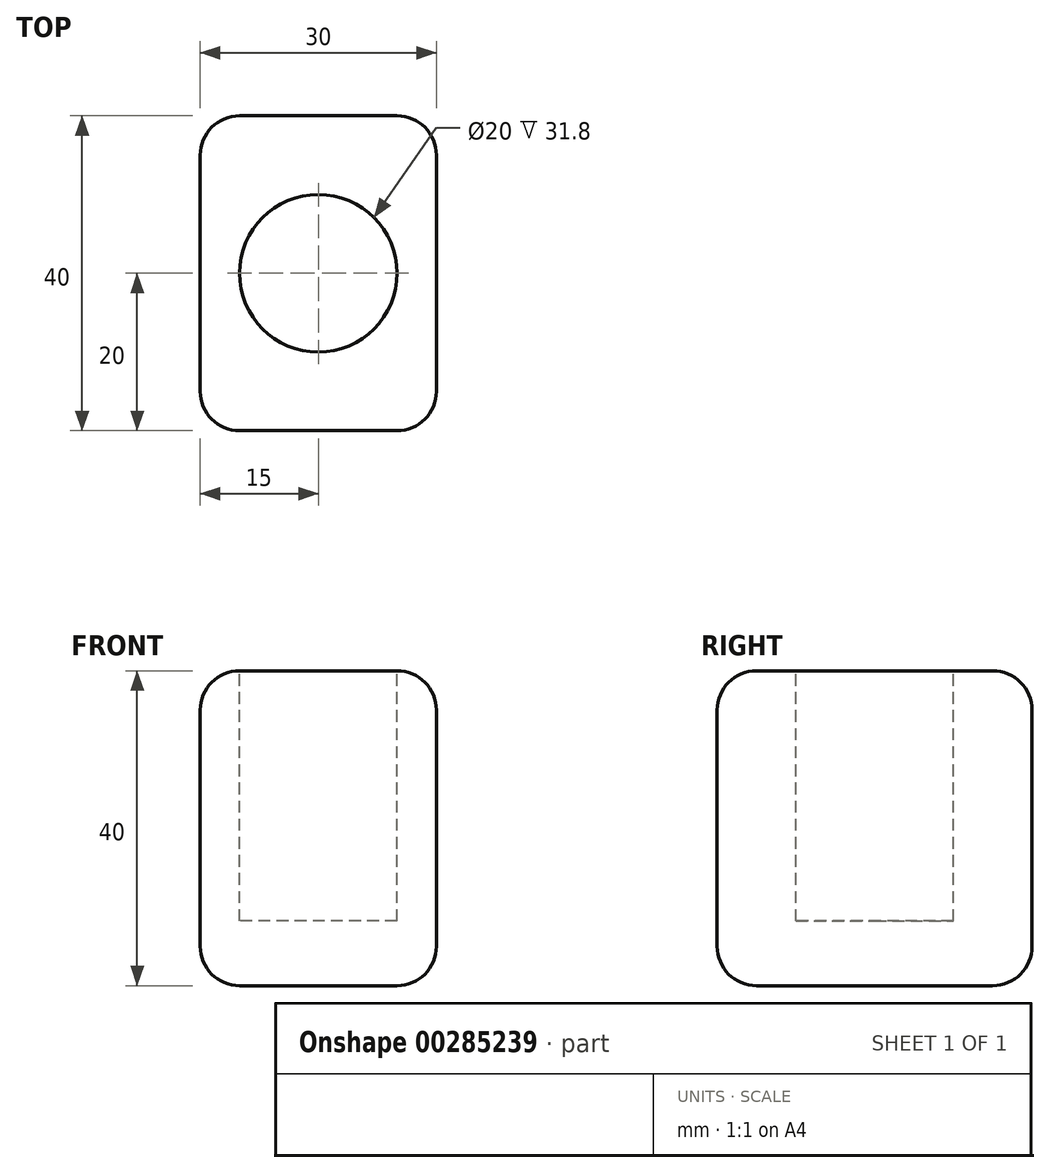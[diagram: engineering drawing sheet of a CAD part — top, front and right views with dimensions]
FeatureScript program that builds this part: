
annotation { "Feature Type Name" : "Feature", "Feature Type Description" : "" }
export const myFeature = defineFeature(function(context is Context, id is Id, definition is map)
    precondition{}
    {
        {
            var Q0;
            Q0=qCreatedBy(makeId("Top.planeOp"),FACE);
            var sketch = newSketch(context, id + "F0", { "sketchPlane" : qUnion([Q0])});
            skLineSegment(sketch, "E0.bottom", {"start": v(0, 0) * mm, "end": v(30, 0) * mm});
            skLineSegment(sketch, "E0.top", {"start": v(0, 40) * mm, "end": v(30, 40) * mm});
            skLineSegment(sketch, "E0.left", {"start": v(0, 0) * mm, "end": v(0, 40) * mm});
            skLineSegment(sketch, "E0.right", {"start": v(30, 0) * mm, "end": v(30, 40) * mm});
            skSolve(sketch);
        }
        {
            var Q0;
            Q0 = qSketchRegion(id + "F0", true);
            extrude(context, id + "F1", {"entities" : qUnion([Q0]), "depth" : 40 * mm});
        }
        {
            var Q0;
            Q0=makeQuery(id+"F1.opExtrude","CAP_FACE",FACE,{"disambiguationData":[OSD([sQuery(id+"F0.wireOp",EDGE,"E0.bottom"),sQuery(id+"F0.wireOp",EDGE,"E0.top"),sQuery(id+"F0.wireOp",EDGE,"E0.left"),sQuery(id+"F0.wireOp",EDGE,"E0.right")])],"isStart":false});
            var sketch = newSketch(context, id + "F2", { "sketchPlane" : qUnion([Q0])});
            skCircle(sketch, "E1", {"center": v(15, 20) * mm, "radius": 10 * mm});
            skPoint(sketch, "E1.centerSnap0", {"position": v(30, 20) * mm});
            skPoint(sketch, "E1.centerSnap1", {"position": v(15, 40) * mm});
            skSolve(sketch);
        }
        {
            var Q0;
            Q0=makeQuery(id+"F1.opExtrude","CAP_FACE",FACE,{"disambiguationData":[OSD([sQuery(id+"F0.wireOp",EDGE,"E0.bottom"),sQuery(id+"F0.wireOp",EDGE,"E0.top"),sQuery(id+"F0.wireOp",EDGE,"E0.left"),sQuery(id+"F0.wireOp",EDGE,"E0.right")])],"isStart":false});
            var sketch = newSketch(context, id + "F3", { "sketchPlane" : qUnion([Q0])});
            skSolve(sketch);
        }
        {
            var Q0;
            Q0 = qSketchRegion(id + "F2", true);
            extrude(context, id + "F4", {"entities" : qUnion([Q0]), "operationType" : NewBodyOperationType.REMOVE, "oppositeDirection" : true, "depth" : 31.8 * mm});
        }
        {
            var Q0;
            Q0=makeQuery(id+"F1.opExtrude","CAP_EDGE",EDGE,{"disambiguationData":[OSD([sQuery(id+"F0.wireOp",EDGE,"E0.bottom")])],"isStart":false});
            var Q1;
            Q1=makeQuery(id+"F1.opExtrude","CAP_EDGE",EDGE,{"disambiguationData":[OSD([sQuery(id+"F0.wireOp",EDGE,"E0.top")])],"isStart":false});
            var Q2;
            Q2=makeQuery(id+"F1.opExtrude","CAP_EDGE",EDGE,{"disambiguationData":[OSD([sQuery(id+"F0.wireOp",EDGE,"E0.right")])],"isStart":false});
            var Q3;
            Q3=makeQuery(id+"F1.opExtrude","CAP_EDGE",EDGE,{"disambiguationData":[OSD([sQuery(id+"F0.wireOp",EDGE,"E0.left")])],"isStart":false});
            var Q4;
            Q4=makeQuery(id+"F1.opExtrude","CAP_EDGE",EDGE,{"disambiguationData":[OSD([sQuery(id+"F0.wireOp",EDGE,"E0.right")])],"isStart":true});
            var Q5;
            Q5=makeQuery(id+"F1.opExtrude","CAP_EDGE",EDGE,{"disambiguationData":[OSD([sQuery(id+"F0.wireOp",EDGE,"E0.bottom")])],"isStart":true});
            var Q6;
            Q6=makeQuery(id+"F1.opExtrude","CAP_EDGE",EDGE,{"disambiguationData":[OSD([sQuery(id+"F0.wireOp",EDGE,"E0.left")])],"isStart":true});
            var Q7;
            Q7=makeQuery(id+"F1.opExtrude","CAP_EDGE",EDGE,{"disambiguationData":[OSD([sQuery(id+"F0.wireOp",EDGE,"E0.top")])],"isStart":true});
            fillet(context, id + "F5", {"entities" : qUnion([Q0, Q1, Q2, Q3, Q4, Q5, Q6, Q7]), "radius" : 5 * mm, "tangentPropagation" : true, "allowEdgeOverflow" : false});
        }
        {
            var Q0;
            Q0=makeQuery(id+"F1.opExtrude","SWEPT_EDGE",EDGE,{"disambiguationData":[OSD([sQuery(id+"F0.wireOp",EDGE,"E0.top"),sQuery(id+"F0.wireOp",EDGE,"E0.right")])]});
            var Q1;
            Q1=makeQuery(id+"F1.opExtrude","SWEPT_FACE",FACE,{"disambiguationData":[OSD([sQuery(id+"F0.wireOp",EDGE,"E0.top")])]});
            var Q2;
            Q2=makeQuery(id+"F1.opExtrude","SWEPT_EDGE",EDGE,{"disambiguationData":[OSD([sQuery(id+"F0.wireOp",EDGE,"E0.bottom"),sQuery(id+"F0.wireOp",EDGE,"E0.left")])]});
            var Q3;
            Q3=makeQuery(id+"F1.opExtrude","SWEPT_EDGE",EDGE,{"disambiguationData":[OSD([sQuery(id+"F0.wireOp",EDGE,"E0.bottom"),sQuery(id+"F0.wireOp",EDGE,"E0.right")])]});
            fillet(context, id + "F6", {"entities" : qUnion([Q0, Q1, Q2, Q3]), "radius" : 5 * mm, "tangentPropagation" : true, "allowEdgeOverflow" : false});
        }
    });
